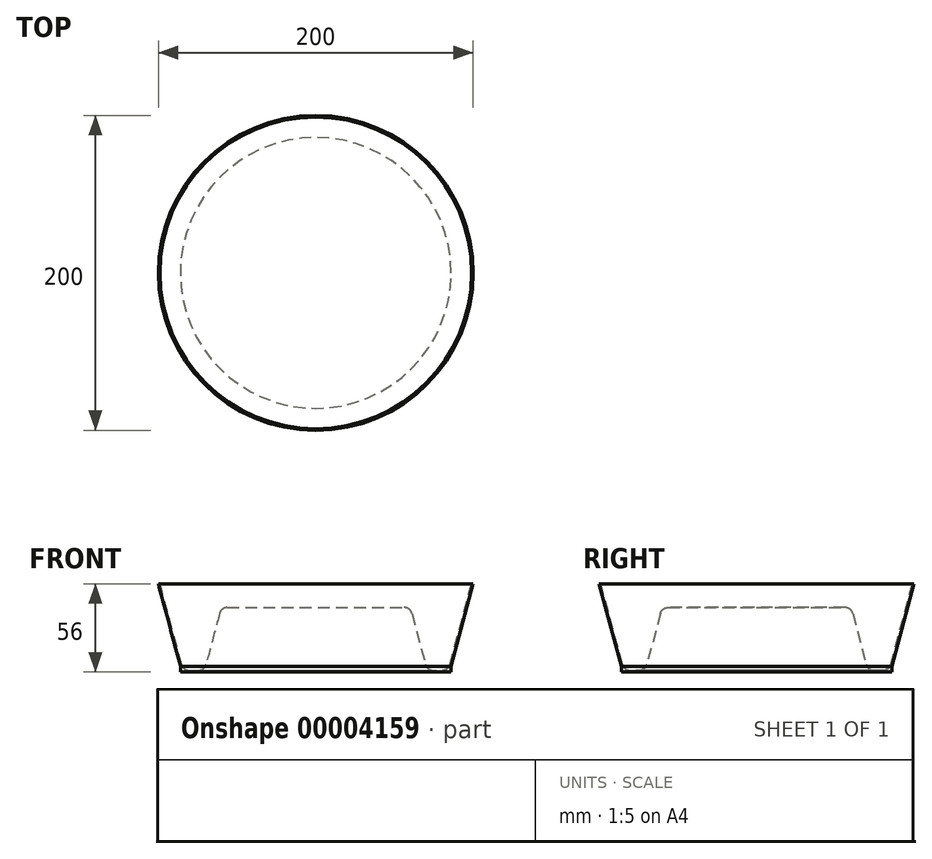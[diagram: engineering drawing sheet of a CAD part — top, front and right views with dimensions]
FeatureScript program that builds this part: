
annotation { "Feature Type Name" : "Feature", "Feature Type Description" : "" }
export const myFeature = defineFeature(function(context is Context, id is Id, definition is map)
    precondition{}
    {
        {
            var Q0;
            Q0=qCreatedBy(makeId("Front.planeOp"),FACE);
            var sketch = newSketch(context, id + "F0", { "sketchPlane" : qUnion([Q0])});
            skLineSegment(sketch, "E0", {"start": v(0, 0) * mm, "end": v(0, 200) * mm, "construction": true});
            skLineSegment(sketch, "E1", {"start": v(0, 40) * mm, "end": v(55.44, 40) * mm});
            skLineSegment(sketch, "E2", {"start": v(60.27, 36.3) * mm, "end": v(69, 3.7) * mm});
            skLineSegment(sketch, "E3", {"start": v(73.83, 0) * mm, "end": v(81.16, 0) * mm});
            skLineSegment(sketch, "E4", {"start": v(85.99, 3.7) * mm, "end": v(100, 56) * mm});
            skLineSegment(sketch, "E5", {"start": v(100, 56) * mm, "end": v(98.96, 56) * mm});
            skLineSegment(sketch, "E6", {"start": v(98.96, 56) * mm, "end": v(85.22, 4.7) * mm});
            skLineSegment(sketch, "E7", {"start": v(80.4, 1) * mm, "end": v(74.6, 1) * mm});
            skLineSegment(sketch, "E8", {"start": v(69.77, 4.7) * mm, "end": v(61.04, 37.3) * mm});
            skLineSegment(sketch, "E9", {"start": v(56.2, 41) * mm, "end": v(0, 41) * mm});
            skLineSegment(sketch, "E10", {"start": v(0, 41) * mm, "end": v(0, 40) * mm});
            skPoint(sketch, "E11.visualSharp", {"position": v(59.28, 40) * mm});
            skArc(sketch, "E11.filletArc", {"start": v(60.27, 36.3) * mm, "mid": v(58.48, 38.97) * mm, "end": v(55.44, 40) * mm});
            skPoint(sketch, "E12.visualSharp", {"position": v(60.04, 41) * mm});
            skArc(sketch, "E12.filletArc", {"start": v(61.04, 37.3) * mm, "mid": v(59.25, 39.97) * mm, "end": v(56.2, 41) * mm});
            skPoint(sketch, "E13.visualSharp", {"position": v(70, 0) * mm});
            skArc(sketch, "E13.filletArc", {"start": v(69, 3.7) * mm, "mid": v(70.79, 1.03) * mm, "end": v(73.83, 0) * mm});
            skPoint(sketch, "E14.visualSharp", {"position": v(70.76, 1) * mm});
            skArc(sketch, "E14.filletArc", {"start": v(69.77, 4.7) * mm, "mid": v(71.56, 2.03) * mm, "end": v(74.6, 1) * mm});
            skPoint(sketch, "E15.visualSharp", {"position": v(84.23, 1) * mm});
            skArc(sketch, "E15.filletArc", {"start": v(80.4, 1) * mm, "mid": v(83.43, 2.03) * mm, "end": v(85.22, 4.7) * mm});
            skPoint(sketch, "E16.visualSharp", {"position": v(85, 0) * mm});
            skArc(sketch, "E16.filletArc", {"start": v(81.16, 0) * mm, "mid": v(84.2, 1.03) * mm, "end": v(85.99, 3.7) * mm});
            skSolve(sketch);
        }
        {
            var Q0;
            Q0 = qSketchRegion(id + "F0", true);
            var Q1;
            Q1=sQuery(id+"F0.wireOp",EDGE,"E0");
            revolve(context, id + "F1", {"entities" : qUnion([Q0]), "axis" : qUnion([Q1]), "revolveType" : RevolveType.FULL});
        }
        {
            var Q0;
            Q0=makeQuery(id+"F1.opRevolve","SWEPT_FACE",FACE,{"disambiguationData":[OSD([sQuery(id+"F0.wireOp",EDGE,"E3")])]});
            var sketch = newSketch(context, id + "F2", { "sketchPlane" : qUnion([Q0])});
            skCircle(sketch, "E17.0", {"center": v(0, 0) * mm, "radius": 85.99 * mm});
            skCircle(sketch, "E18.0", {"center": v(0, 0) * mm, "radius": 81.16 * mm});
            skCircle(sketch, "E19.0", {"center": v(0, 0) * mm, "radius": 73.83 * mm});
            skSolve(sketch);
        }
        {
            var Q0;
            Q0 = qSketchRegion(id + "F2", true);
            var Q1;
            Q1=makeQuery(id+"F2.imprint","IMPRINT",FACE,{"disambiguationData":[TD([[makeQuery(id+"F2.imprint","IMPRINT",EDGE,{"derivedFrom":sQuery(id+"F2.wireOp",EDGE,"E19.0")}),1.0]])]});
            extrude(context, id + "F3", {"entities" : qUnion([Q0, Q1]), "operationType" : NewBodyOperationType.ADD, "endBound" : BoundingType.UP_TO_NEXT, "oppositeDirection" : true, "depth" : 25 * mm});
        }
    });
